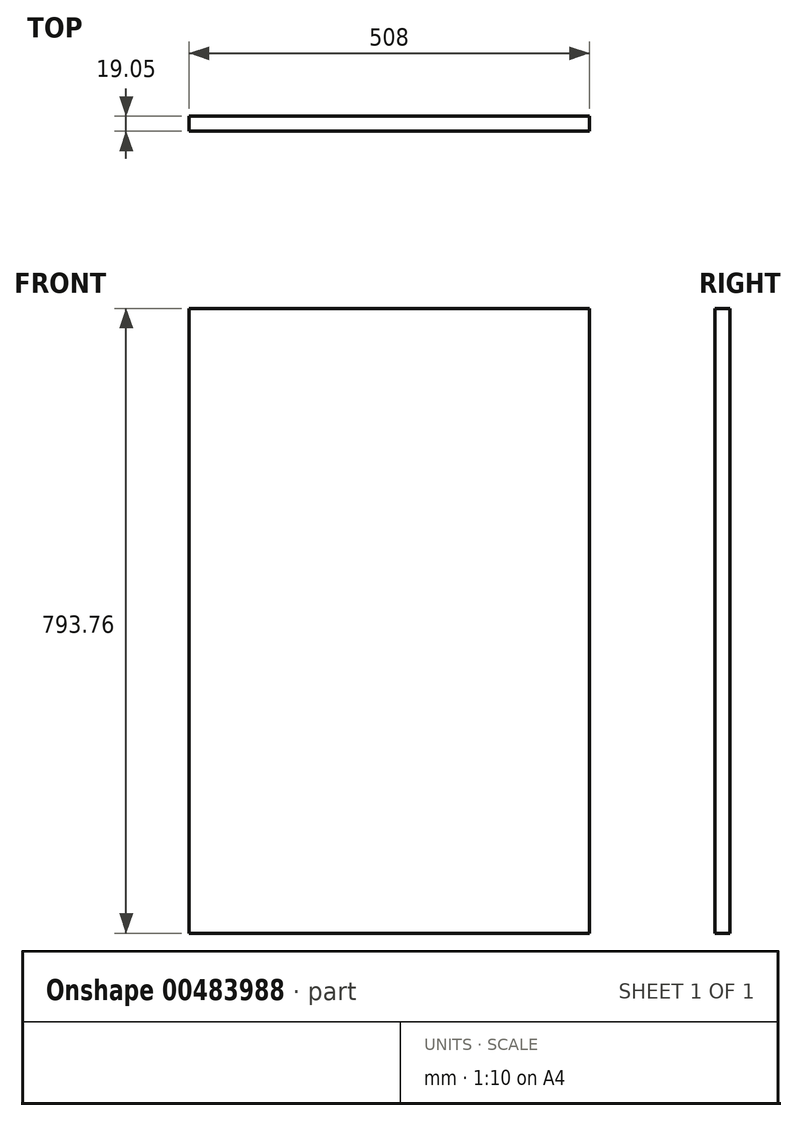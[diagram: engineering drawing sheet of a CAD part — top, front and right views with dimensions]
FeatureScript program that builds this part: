
annotation { "Feature Type Name" : "Feature", "Feature Type Description" : "" }
export const myFeature = defineFeature(function(context is Context, id is Id, definition is map)
    precondition{}
    {
        {
            var Q0;
            Q0=qCreatedBy(makeId("Front.planeOp"),FACE);
            var sketch = newSketch(context, id + "F0", { "sketchPlane" : qUnion([Q0])});
            skLineSegment(sketch, "E0.bottom", {"start": v(254, 396.88) * mm, "end": v(-254, 396.88) * mm});
            skLineSegment(sketch, "E0.top", {"start": v(254, -396.88) * mm, "end": v(-254, -396.88) * mm});
            skLineSegment(sketch, "E0.left", {"start": v(254, 396.88) * mm, "end": v(254, -396.88) * mm});
            skLineSegment(sketch, "E0.right", {"start": v(-254, 396.88) * mm, "end": v(-254, -396.88) * mm});
            skPoint(sketch, "E0.middle", {"position": v(0, 0) * mm});
            skSolve(sketch);
        }
        {
            var Q0;
            Q0 = qSketchRegion(id + "F0", true);
            extrude(context, id + "F1", {"entities" : qUnion([Q0]), "depth" : 19.05 * mm});
        }
    });
